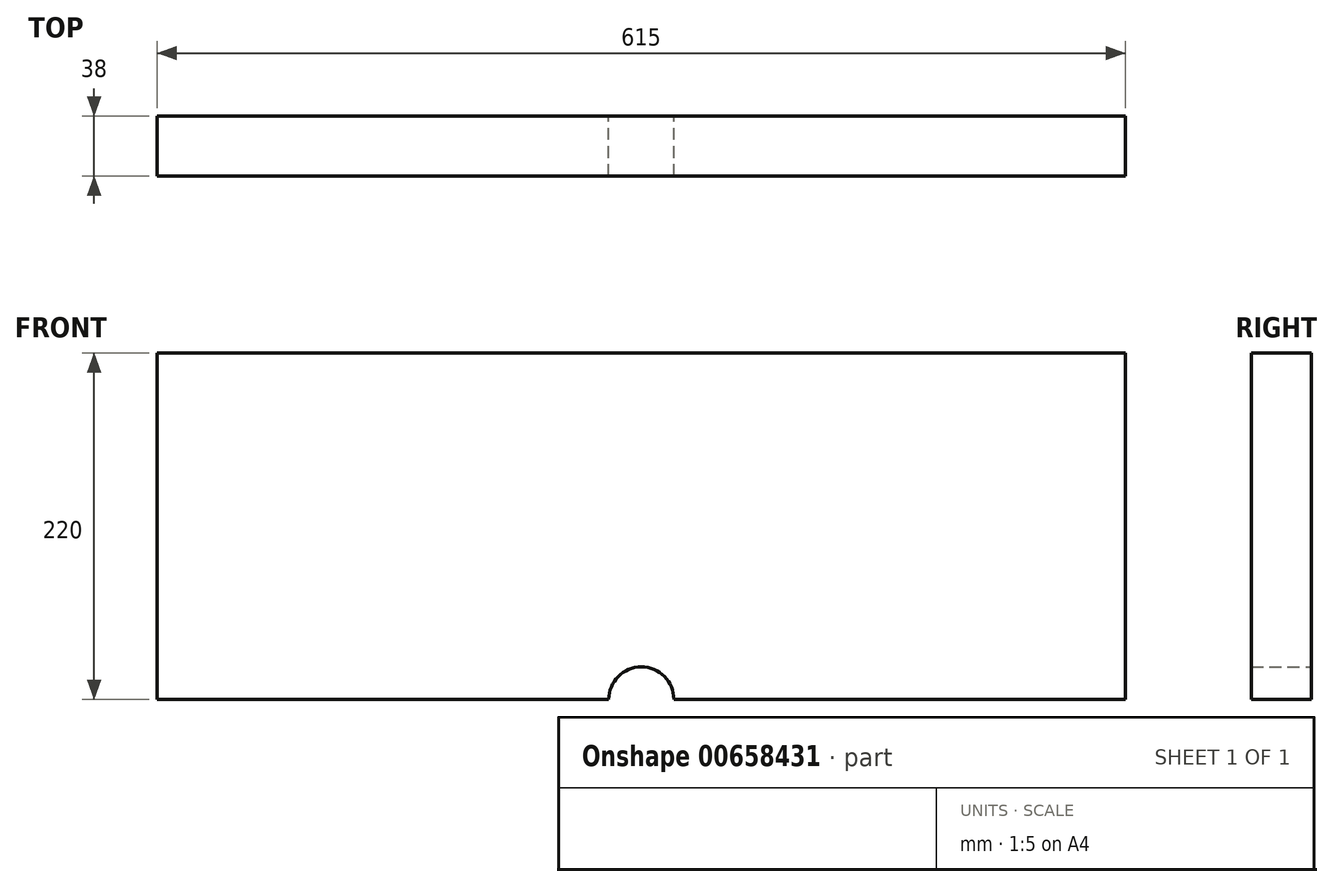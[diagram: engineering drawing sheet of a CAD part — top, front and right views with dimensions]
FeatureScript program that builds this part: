
annotation { "Feature Type Name" : "Feature", "Feature Type Description" : "" }
export const myFeature = defineFeature(function(context is Context, id is Id, definition is map)
    precondition{}
    {
        {
            var Q0;
            Q0=qCreatedBy(makeId("Front.planeOp"),FACE);
            var sketch = newSketch(context, id + "F0", { "sketchPlane" : qUnion([Q0])});
            skLineSegment(sketch, "E0.bottom", {"start": v(-305.2, 104.16) * mm, "end": v(309.8, 104.16) * mm});
            skLineSegment(sketch, "E0.top", {"start": v(-305.2, -115.84) * mm, "end": v(-18.38, -115.84) * mm});
            skLineSegment(sketch, "E0.left", {"start": v(-305.2, 104.16) * mm, "end": v(-305.2, -115.84) * mm});
            skLineSegment(sketch, "E0.right", {"start": v(309.8, 104.16) * mm, "end": v(309.8, -115.84) * mm});
            skPoint(sketch, "E1.center.orphan", {"position": v(2.3, -143.42) * mm});
            skLineSegment(sketch, "E2", {"start": v(2.3, 104.16) * mm, "end": v(2.3, -115.84) * mm, "construction": true});
            skArc(sketch, "E3", {"start": v(22.98, -115.84) * mm, "mid": v(2.3, -95.16) * mm, "end": v(-18.38, -115.84) * mm});
            skLineSegment(sketch, "E4.trimOffspring", {"start": v(22.98, -115.84) * mm, "end": v(309.8, -115.84) * mm});
            skSolve(sketch);
        }
        {
            var Q0;
            Q0=makeQuery(id+"F0.imprint","IMPRINT",FACE,{"disambiguationData":[TD([[makeQuery(id+"F0.imprint","IMPRINT",EDGE,{"derivedFrom":sQuery(id+"F0.wireOp",EDGE,"E0.bottom")}),-1.0]])]});
            extrude(context, id + "F1", {"entities" : qUnion([Q0]), "depth" : 38 * mm, "offsetDistance" : 25 * mm});
        }
    });
